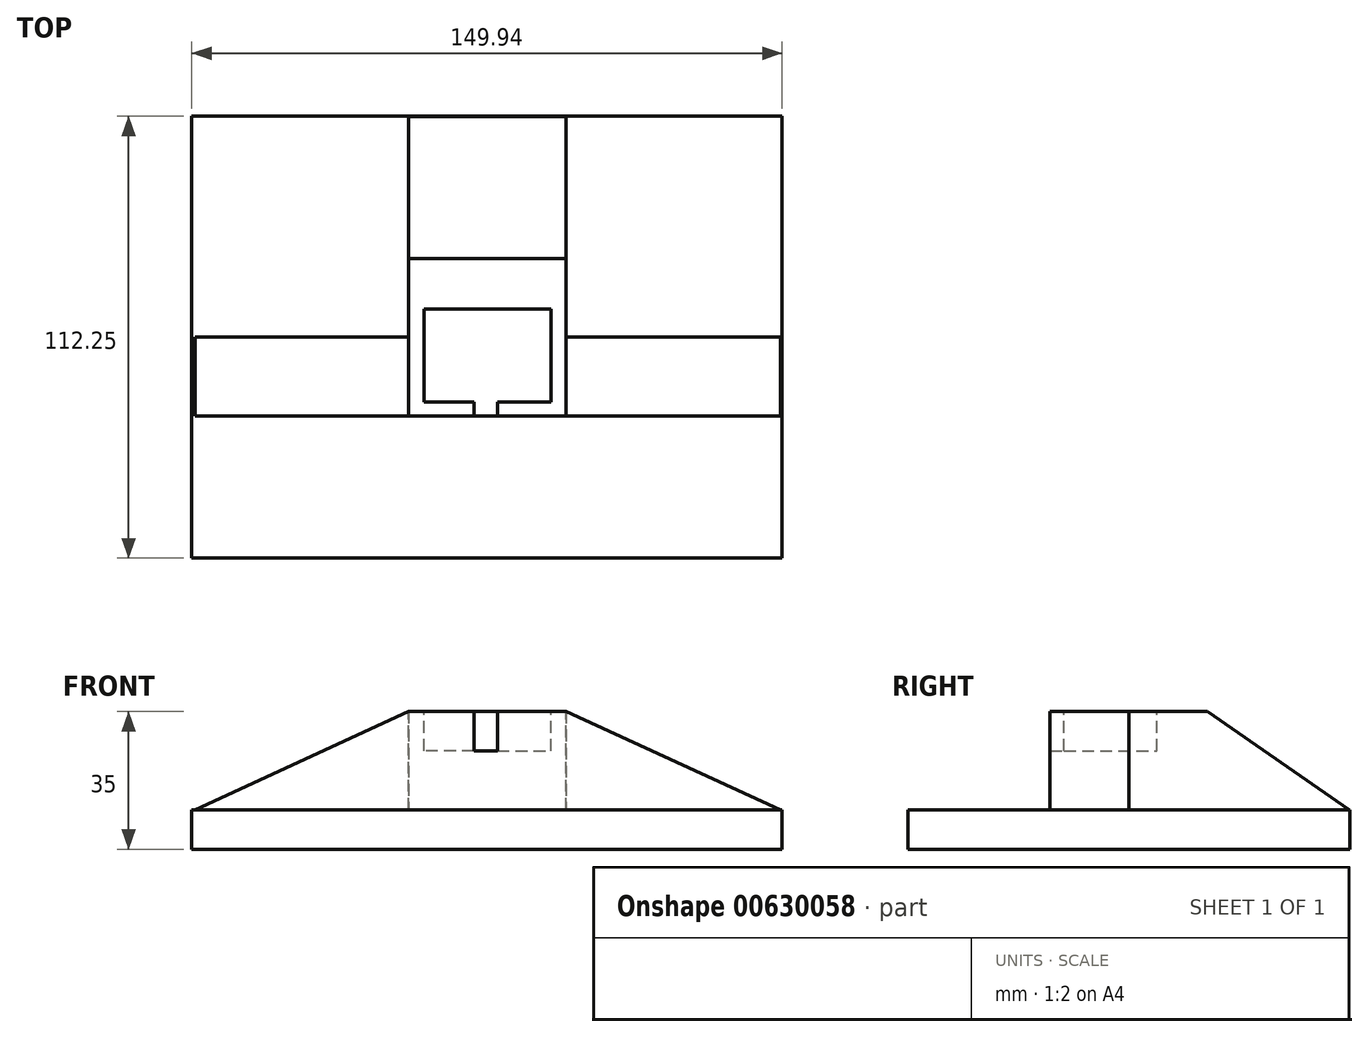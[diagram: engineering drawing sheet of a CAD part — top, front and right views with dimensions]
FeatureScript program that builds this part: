
annotation { "Feature Type Name" : "Feature", "Feature Type Description" : "" }
export const myFeature = defineFeature(function(context is Context, id is Id, definition is map)
    precondition{}
    {
        {
            var Q0;
            Q0=qCreatedBy(makeId("Top.planeOp"),FACE);
            var sketch = newSketch(context, id + "F0", { "sketchPlane" : qUnion([Q0])});
            skLineSegment(sketch, "E0.bottom", {"start": v(-74.97, 56.27) * mm, "end": v(74.97, 56.27) * mm});
            skLineSegment(sketch, "E0.top", {"start": v(-74.97, -55.98) * mm, "end": v(74.97, -55.98) * mm});
            skLineSegment(sketch, "E0.left", {"start": v(-74.97, 56.27) * mm, "end": v(-74.97, -55.98) * mm});
            skLineSegment(sketch, "E0.right", {"start": v(74.97, 56.27) * mm, "end": v(74.97, -55.98) * mm});
            skSolve(sketch);
        }
        {
            var Q0;
            Q0=qSketchRegion(id+"F0",true);
            extrude(context, id + "F1", {"entities" : qUnion([Q0]), "depth" : 10 * mm, "offsetDistance" : 25 * mm});
        }
        {
            var Q0;
            Q0=makeQuery(id+"F1.opExtrude","CAP_FACE",FACE,{"disambiguationData":[OSD([sQuery(id+"F0.wireOp",EDGE,"E0.bottom"),sQuery(id+"F0.wireOp",EDGE,"E0.top"),sQuery(id+"F0.wireOp",EDGE,"E0.left"),sQuery(id+"F0.wireOp",EDGE,"E0.right")])],"isStart":false});
            var sketch = newSketch(context, id + "F2", { "sketchPlane" : qUnion([Q0])});
            skLineSegment(sketch, "E1", {"start": v(0, 0) * mm, "end": v(0, 20.14) * mm});
            skLineSegment(sketch, "E2", {"start": v(0, 20.14) * mm, "end": v(20.14, 20.14) * mm});
            skLineSegment(sketch, "E3", {"start": v(20.14, 20.14) * mm, "end": v(20.14, -19.86) * mm});
            skLineSegment(sketch, "E4", {"start": v(20.14, -19.86) * mm, "end": v(-19.86, -19.86) * mm});
            skLineSegment(sketch, "E5", {"start": v(-19.86, -19.86) * mm, "end": v(-19.86, 20.14) * mm});
            skLineSegment(sketch, "E6", {"start": v(-19.86, 20.14) * mm, "end": v(0, 20.14) * mm});
            skSolve(sketch);
        }
        {
            var Q0;
            Q0=qSketchRegion(id+"F2",true);
            extrude(context, id + "F3", {"entities" : qUnion([Q0]), "operationType" : NewBodyOperationType.ADD, "depth" : 25 * mm, "offsetDistance" : 25 * mm});
        }
        {
            var Q0;
            Q0=makeQuery(id+"F3.opExtrude","CAP_FACE",FACE,{"disambiguationData":[OSD([sQuery(id+"F2.wireOp",EDGE,"E2"),sQuery(id+"F2.wireOp",EDGE,"E3"),sQuery(id+"F2.wireOp",EDGE,"E4"),sQuery(id+"F2.wireOp",EDGE,"E5"),sQuery(id+"F2.wireOp",EDGE,"E6")])],"isStart":false});
            var sketch = newSketch(context, id + "F4", { "sketchPlane" : qUnion([Q0])});
            skLineSegment(sketch, "E7", {"start": v(-16, 7.22) * mm, "end": v(-16, -16.29) * mm});
            skLineSegment(sketch, "E8", {"start": v(-16, -16.29) * mm, "end": v(16.29, -16.29) * mm});
            skLineSegment(sketch, "E9", {"start": v(16.29, -16.29) * mm, "end": v(-16, 7.22) * mm});
            skLineSegment(sketch, "E10", {"start": v(16.29, -16.29) * mm, "end": v(16.29, 7.22) * mm});
            skLineSegment(sketch, "E11", {"start": v(16.29, 7.22) * mm, "end": v(-16, 7.22) * mm});
            skLineSegment(sketch, "E12", {"start": v(-3.26, -19.86) * mm, "end": v(-3.26, -16.29) * mm});
            skLineSegment(sketch, "E13", {"start": v(-3.26, -16.29) * mm, "end": v(2.7, -16.29) * mm});
            skLineSegment(sketch, "E14", {"start": v(2.7, -16.29) * mm, "end": v(2.7, -19.86) * mm});
            skLineSegment(sketch, "E15", {"start": v(2.7, -19.86) * mm, "end": v(-3.26, -19.86) * mm});
            skLineSegment(sketch, "E16", {"start": v(-3.26, -19.86) * mm, "end": v(2.7, -19.86) * mm});
            skSolve(sketch);
        }
        {
            var Q0;
            Q0=qSketchRegion(id+"F4",true);
            extrude(context, id + "F5", {"entities" : qUnion([Q0]), "operationType" : NewBodyOperationType.REMOVE, "oppositeDirection" : true, "depth" : 10 * mm, "offsetDistance" : 25 * mm});
        }
        {
            var Q0;
            Q0=makeQuery(id+"F3.opExtrude","SWEPT_FACE",FACE,{"disambiguationData":[OSD([sQuery(id+"F2.wireOp",EDGE,"E4")])]});
            var sketch = newSketch(context, id + "F6", { "sketchPlane" : qUnion([Q0])});
            skLineSegment(sketch, "E17", {"start": v(20.14, 35) * mm, "end": v(74.64, 10.06) * mm});
            skLineSegment(sketch, "E18", {"start": v(-19.86, 35) * mm, "end": v(-74.64, 9.77) * mm});
            skLineSegment(sketch, "E19", {"start": v(20.14, 35) * mm, "end": v(20.14, 10) * mm});
            skLineSegment(sketch, "E20", {"start": v(20.14, 10) * mm, "end": v(74.64, 10.06) * mm});
            skLineSegment(sketch, "E21", {"start": v(-19.86, 35) * mm, "end": v(-19.86, 10) * mm});
            skLineSegment(sketch, "E22", {"start": v(-19.86, 10) * mm, "end": v(-74.64, 9.77) * mm});
            skSolve(sketch);
        }
        {
            var Q0;
            Q0=qSketchRegion(id+"F6",true);
            extrude(context, id + "F7", {"entities" : qUnion([Q0]), "operationType" : NewBodyOperationType.ADD, "oppositeDirection" : true, "depth" : 20 * mm, "offsetDistance" : 25 * mm});
        }
        {
            var Q0;
            Q0=makeQuery(id+"F3.opExtrude","SWEPT_FACE",FACE,{"disambiguationData":[OSD([sQuery(id+"F2.wireOp",EDGE,"E5")])]});
            var sketch = newSketch(context, id + "F8", { "sketchPlane" : qUnion([Q0])});
            skLineSegment(sketch, "E23", {"start": v(-56.23, 10.06) * mm, "end": v(-20.14, 35) * mm});
            skLineSegment(sketch, "E24", {"start": v(-20.14, 35) * mm, "end": v(-20.14, 10) * mm});
            skLineSegment(sketch, "E25", {"start": v(-20.14, 10) * mm, "end": v(-56.23, 10.06) * mm});
            skSolve(sketch);
        }
        {
            var Q0;
            Q0=qSketchRegion(id+"F8",true);
            extrude(context, id + "F9", {"entities" : qUnion([Q0]), "operationType" : NewBodyOperationType.ADD, "oppositeDirection" : true, "depth" : 40 * mm, "offsetDistance" : 25 * mm});
        }
    });
